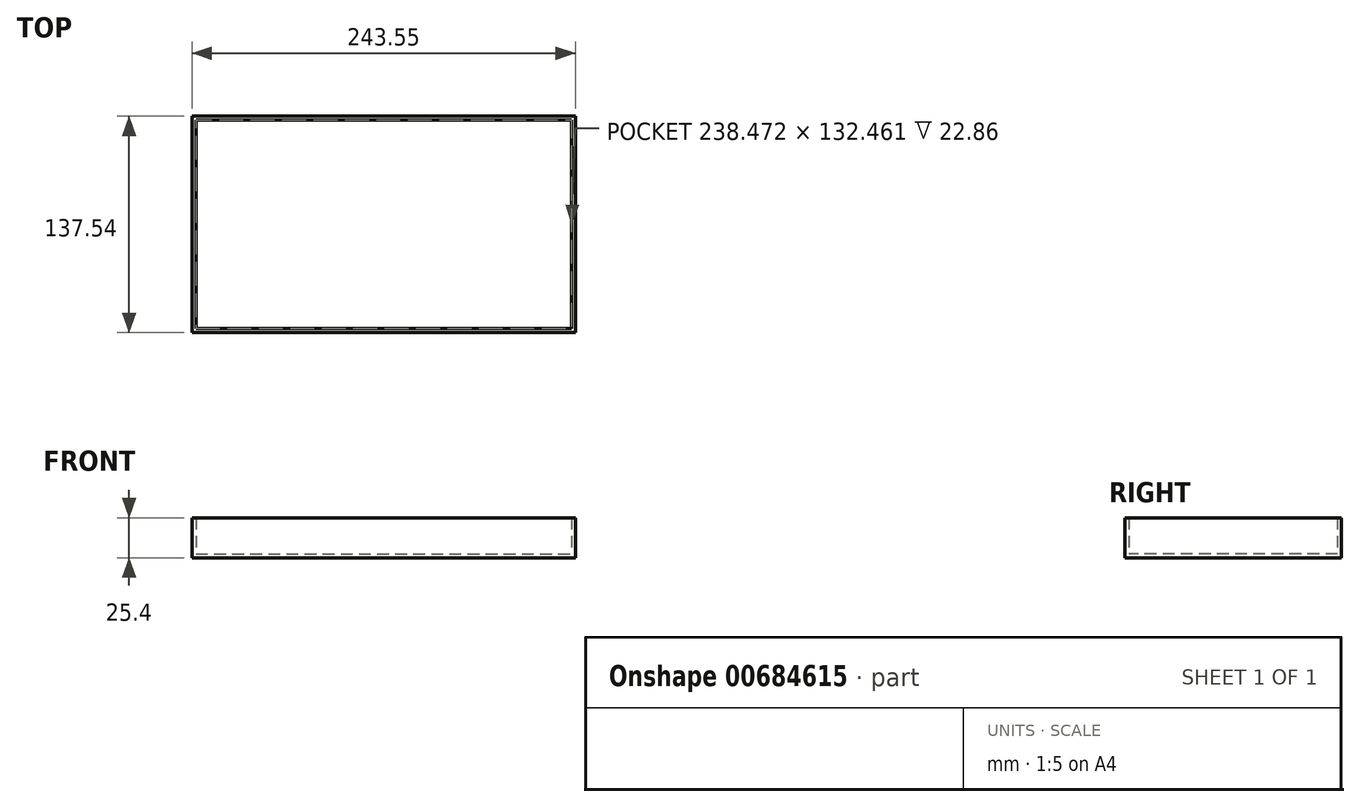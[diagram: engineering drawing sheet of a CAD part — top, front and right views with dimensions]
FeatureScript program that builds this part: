
annotation { "Feature Type Name" : "Feature", "Feature Type Description" : "" }
export const myFeature = defineFeature(function(context is Context, id is Id, definition is map)
    precondition{}
    {
        {
            var Q0;
            Q0=qCreatedBy(makeId("Top.planeOp"),FACE);
            var sketch = newSketch(context, id + "F0", { "sketchPlane" : qUnion([Q0])});
            skLineSegment(sketch, "E0.bottom", {"start": v(-129.22, 58.4) * mm, "end": v(114.33, 58.4) * mm});
            skLineSegment(sketch, "E0.top", {"start": v(-129.22, -79.13) * mm, "end": v(114.33, -79.13) * mm});
            skLineSegment(sketch, "E0.left", {"start": v(-129.22, 58.4) * mm, "end": v(-129.22, -79.13) * mm});
            skLineSegment(sketch, "E0.right", {"start": v(114.33, 58.4) * mm, "end": v(114.33, -79.13) * mm});
            skLineSegment(sketch, "E1", {"start": v(0, 72.99) * mm, "end": v(0, -136.57) * mm, "construction": true});
            skSolve(sketch);
        }
        {
            var Q0;
            Q0=makeQuery(id+"F0.imprint","IMPRINT",FACE,{"disambiguationData":[TD([[makeQuery(id+"F0.imprint","IMPRINT",EDGE,{"derivedFrom":sQuery(id+"F0.wireOp",EDGE,"E0.bottom")}),-1.0]])]});
            extrude(context, id + "F1", {"entities" : qUnion([Q0]), "depth" : 25.4 * mm, "offsetDistance" : 25.4 * mm});
        }
        {
            var Q0;
            Q0=makeQuery(id+"F1.opExtrude","CAP_FACE",FACE,{"disambiguationData":[OSD([sQuery(id+"F0.wireOp",EDGE,"E0.bottom"),sQuery(id+"F0.wireOp",EDGE,"E0.top"),sQuery(id+"F0.wireOp",EDGE,"E0.left"),sQuery(id+"F0.wireOp",EDGE,"E0.right")])],"isStart":false});
            shell(context, id + "F2", {"entities" : qUnion([Q0]), "thickness" : 2.54 * mm});
        }
    });
